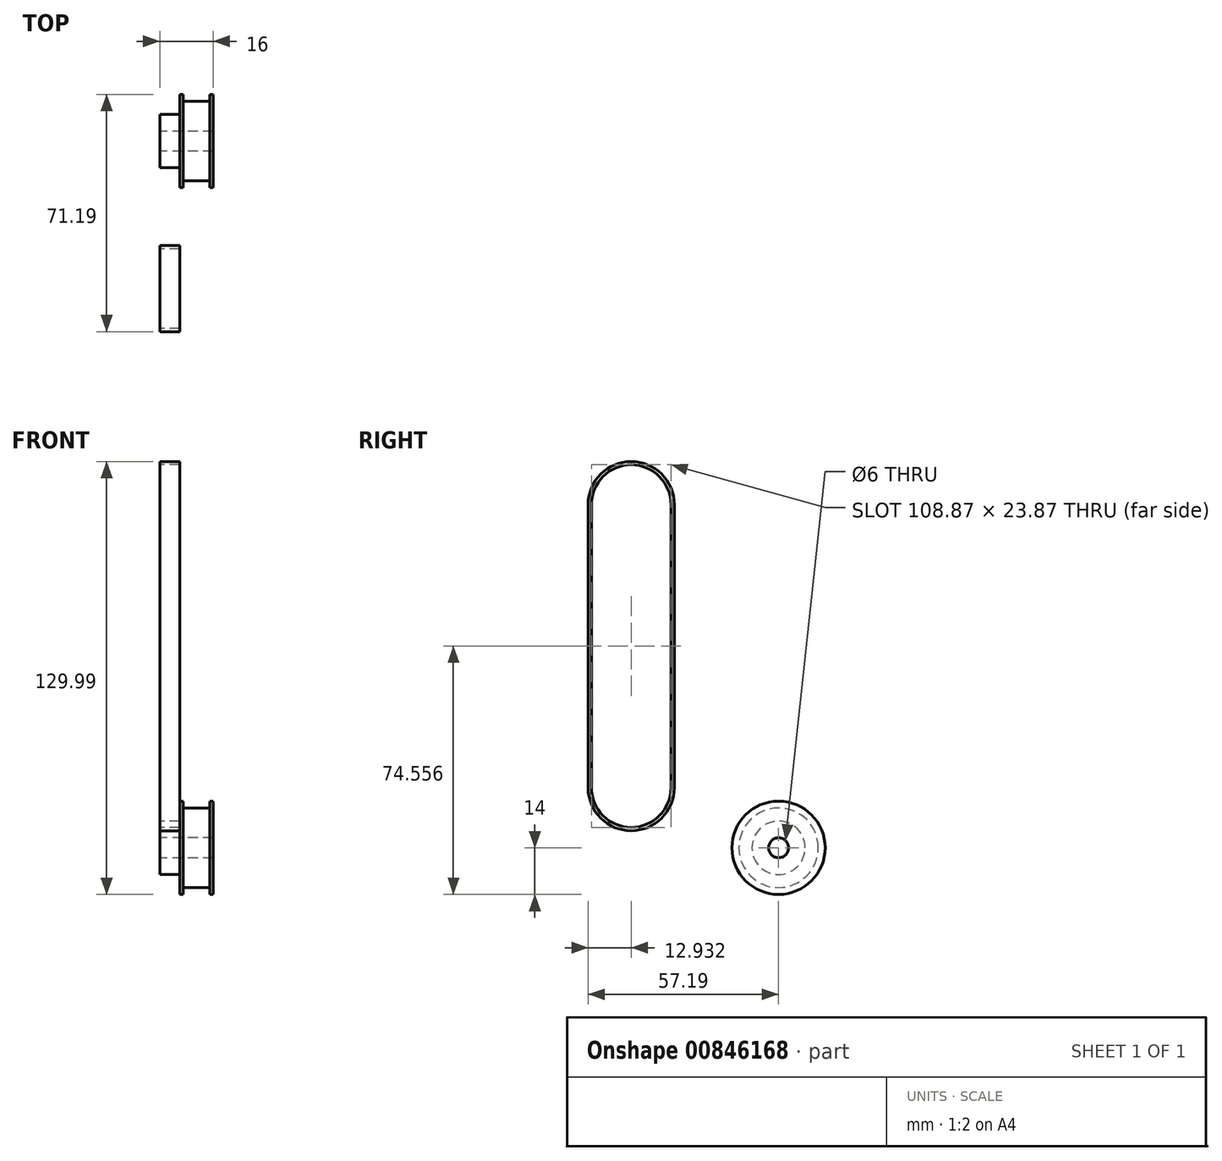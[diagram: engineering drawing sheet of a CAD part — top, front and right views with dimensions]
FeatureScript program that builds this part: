
annotation { "Feature Type Name" : "Feature", "Feature Type Description" : "" }
export const myFeature = defineFeature(function(context is Context, id is Id, definition is map)
    precondition{}
    {
        {
            var Q0;
            Q0=qCreatedBy(makeId("Front.planeOp"),FACE);
            var sketch = newSketch(context, id + "F0", { "sketchPlane" : qUnion([Q0])});
            skLineSegment(sketch, "E0", {"start": v(0, 3) * mm, "end": v(16, 3) * mm});
            skLineSegment(sketch, "E1", {"start": v(16, 3) * mm, "end": v(16, 11.94) * mm});
            skLineSegment(sketch, "E2", {"start": v(6, 11.94) * mm, "end": v(6, 8) * mm});
            skLineSegment(sketch, "E3", {"start": v(6, 8) * mm, "end": v(0, 8) * mm});
            skLineSegment(sketch, "E4", {"start": v(0, 8) * mm, "end": v(0, 3) * mm});
            skLineSegment(sketch, "E5.top", {"start": v(6, 14) * mm, "end": v(7, 14) * mm});
            skLineSegment(sketch, "E5.left", {"start": v(6, 11.94) * mm, "end": v(6, 14) * mm});
            skLineSegment(sketch, "E5.right", {"start": v(7, 11.94) * mm, "end": v(7, 14) * mm});
            skLineSegment(sketch, "E6.top", {"start": v(16, 14) * mm, "end": v(15, 14) * mm});
            skLineSegment(sketch, "E6.left", {"start": v(16, 11.94) * mm, "end": v(16, 14) * mm});
            skLineSegment(sketch, "E6.right", {"start": v(15, 11.94) * mm, "end": v(15, 14) * mm});
            skLineSegment(sketch, "E7", {"start": v(7, 11.94) * mm, "end": v(15, 11.94) * mm});
            skLineSegment(sketch, "E8", {"start": v(3.01, 0) * mm, "end": v(12.2, 0) * mm, "construction": true});
            skSolve(sketch);
        }
        {
            var Q0;
            Q0 = qSketchRegion(id + "F0", true);
            var Q1;
            Q1=sQuery(id+"F0.wireOp",EDGE,"E8");
            revolve(context, id + "F1", {"surfaceOperationType" : NewSurfaceOperationType.NEW, "entities" : qUnion([Q0]), "axis" : qUnion([Q1]), "revolveType" : RevolveType.FULL});
        }
        {
            var Q0;
            Q0=qCreatedBy(makeId("Right.planeOp"),FACE);
            var sketch = newSketch(context, id + "F2", { "sketchPlane" : qUnion([Q0])});
            skLineSegment(sketch, "E9", {"start": v(-56.2, 18.06) * mm, "end": v(-56.2, 103.06) * mm});
            skArc(sketch, "E10", {"start": v(-32.32, 103.06) * mm, "mid": v(-44.26, 115) * mm, "end": v(-56.2, 103.06) * mm});
            skLineSegment(sketch, "E11", {"start": v(-32.32, 103.06) * mm, "end": v(-32.32, 18.06) * mm});
            skArc(sketch, "E12", {"start": v(-56.2, 18.06) * mm, "mid": v(-44.26, 6.12) * mm, "end": v(-32.32, 18.06) * mm});
            skArc(sketch, "E13.0", {"start": v(-31.32, 103.06) * mm, "mid": v(-44.26, 116) * mm, "end": v(-57.2, 103.06) * mm});
            skLineSegment(sketch, "E13.1", {"start": v(-31.32, 103.06) * mm, "end": v(-31.32, 18.06) * mm});
            skArc(sketch, "E13.2", {"start": v(-57.2, 18.06) * mm, "mid": v(-44.26, 5.12) * mm, "end": v(-31.32, 18.06) * mm});
            skLineSegment(sketch, "E13.3", {"start": v(-57.2, 18.06) * mm, "end": v(-57.2, 103.06) * mm});
            skSolve(sketch);
        }
        {
            var Q0;
            Q0=makeQuery(id+"F2.imprint","IMPRINT",FACE,{"disambiguationData":[TD([[makeQuery(id+"F2.imprint","IMPRINT",EDGE,{"derivedFrom":sQuery(id+"F2.wireOp",EDGE,"E9")}),1.0]])]});
            extrude(context, id + "F3", {"entities" : qUnion([Q0]), "depth" : 6 * mm, "offsetDistance" : 25 * mm});
        }
    });
